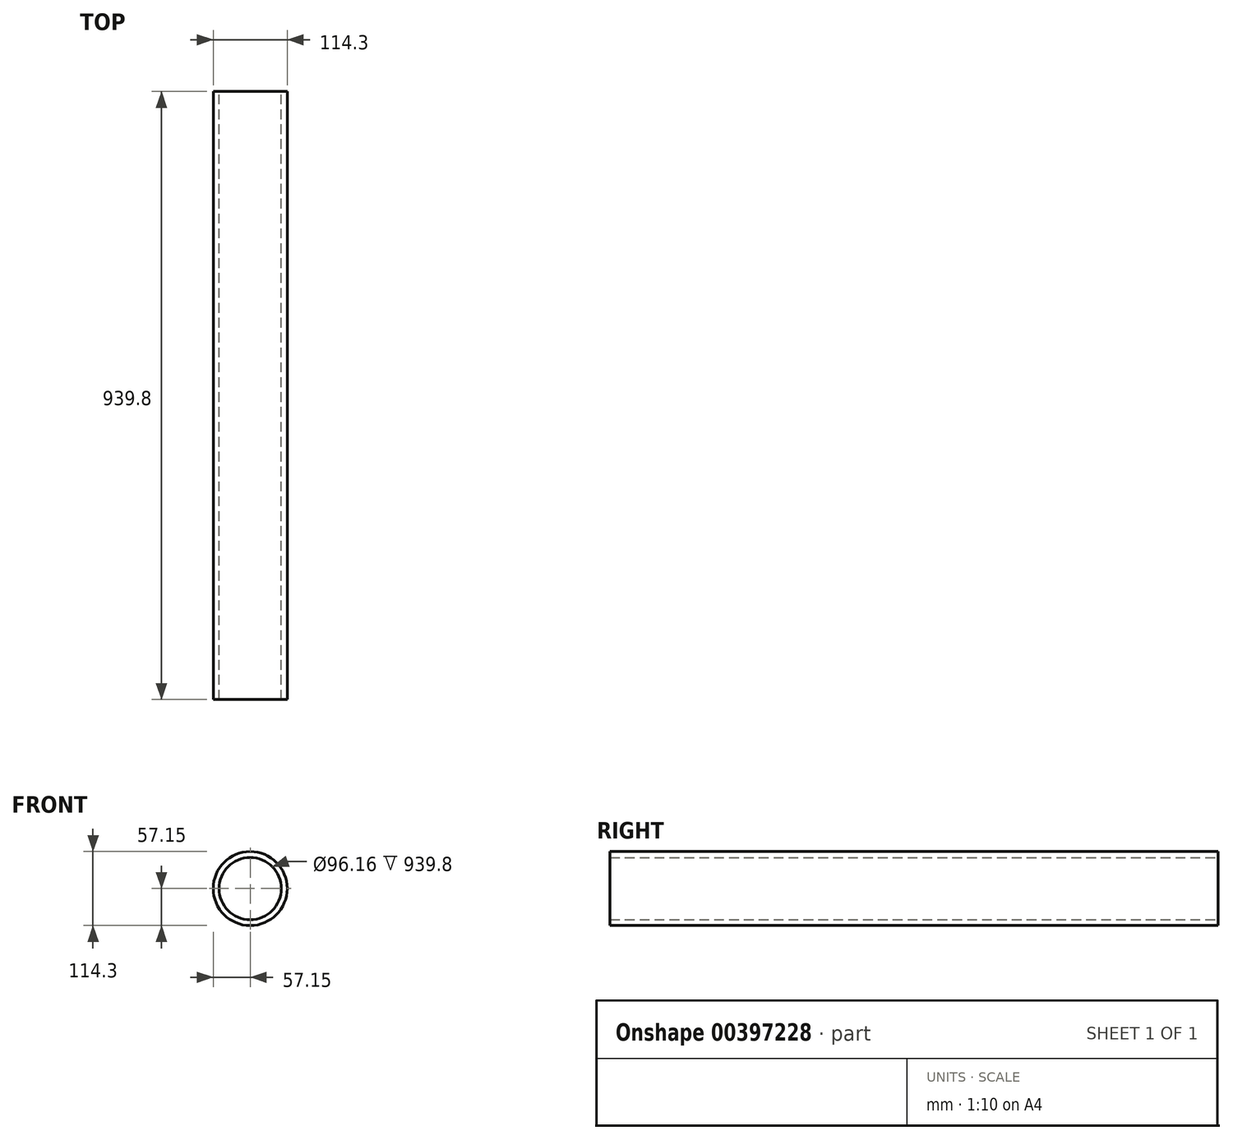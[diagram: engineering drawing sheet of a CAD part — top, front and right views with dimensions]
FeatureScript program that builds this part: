
annotation { "Feature Type Name" : "Feature", "Feature Type Description" : "" }
export const myFeature = defineFeature(function(context is Context, id is Id, definition is map)
    precondition{}
    {
        {
            var Q0;
            Q0=qCreatedBy(makeId("Front.planeOp"),FACE);
            var sketch = newSketch(context, id + "F0", { "sketchPlane" : qUnion([Q0])});
            skCircle(sketch, "E0", {"center": v(0, 0) * mm, "radius": 57.15 * mm});
            skCircle(sketch, "E1", {"center": v(0, 0) * mm, "radius": 48.08 * mm});
            skSolve(sketch);
        }
        {
            var Q0;
            Q0=qSketchRegion(id+"F0",true);
            extrude(context, id + "F1", {"entities" : qUnion([Q0]), "depth" : 939.8 * mm});
        }
        {
            var Q0;
            Q0=qCreatedBy(makeId("Front.planeOp"),FACE);
            var sketch = newSketch(context, id + "F2", { "sketchPlane" : qUnion([Q0])});
            skLineSegment(sketch, "E2", {"start": v(0, 0) * mm, "end": v(-96.2, 0) * mm, "construction": true});
            skSolve(sketch);
        }
    });
